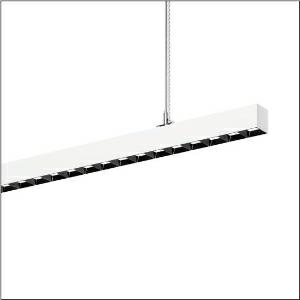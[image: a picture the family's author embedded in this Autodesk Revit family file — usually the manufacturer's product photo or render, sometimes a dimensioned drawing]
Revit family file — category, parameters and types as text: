
# Revit family: silica_r__21_51mx34dc3dwb_cbfc
name_source: partatom
category: Lighting Fixtures
units: mm (PartAtom-declared; Revit-internal decimal feet)

## family parameters
Cut with Voids When Loaded = No
Host = Face
Light Source = No
Part Type = Normal
Room Calculation Point = No
Round Connector Dimension = Use Diameter
Shared = No

## types (1)
- --- (1 x LED, 19200 lm, 129.1 W, 3000K)
    Apparent Load = 129 VA
    CIE Flux Codes = 74 94 99 56 100
    Color Rendering = 80
    Color Temperature = 3000K
    Default Elevation = 1800 mm
    Description = Silica® 21, office luminaire, primary light control with darklight reflector, of PMMA, black, light emission: direct/indirect distribution, primary light characteristic: asymmetric, installation type: suspended mounting, LED, rated luminous flux: 19.200lm, luminous efficacy: 149lm/W, light colour: 830, colour temperature: 3000K, control gear: DALI 2, with terminal, 3+2-pole, max. 2.5mm², mains connection: 220..240V, AC, 50/60Hz, rated input power: 129.1W, luminaire housing, of aluminium, traffic white (RAL 9016), length: 3.004mm, width: 53mm, height: 53mm, protection rating (complete): IP20, insulation class (complete): insulation class I (protective earthing), certification: CE, permissible operating ambient temperature: 0..+35°C, standard: EN 50419, packaging unit: 1 piece
    Height = 53 mm
    Lamp = 1 x LED
    Lamp Light Flux = 19200 lm
    Lamp Power = 129.1 W
    Lamp count = 1
    Length = 3004 mm
    Luminous efficacy = 149 lm/W
    Manufacturer = Siteco
    ModVariant = No
    Model = 51MX34DC3DWB
    Mounting Place = Ceiling
    Mounting Type = Pendant
    Number of Poles = 1
    OnlyDefault = Yes
    Power Factor = 1
    Product Name = Silica® 21
    Product group = office luminaire | ceiling pendant
    ProductGroupID = 903
    Protection Class = Protection class I
    Protection Degree = IP 20
    RLX_Detail_Level = 1
    RLX_Emergency_Light_Flux = 0 lm
    RLX_Emergency_Type = 0
    RLX_Emergency_Type_DB = No
    RlxData = <blob elided: 65373 chars, md5=e60156b5>
    Socket = socket
    Standby Power = 0 W
    System Light Flux = 19200 lm
    System Power = 129 W
    Type Comments = factory setting: luminous flux: 100 % | dim-lin: 254 | 448 mA
    Type Image = l_1335871.jpg
    URL = http://relux.com
    VarID = @adj_141783
    Voltage = 0 V
    Weight = 0.00 kg
    Width = 53 mm

## geometry (parser evidence)
native form markers: Blend x4, Sweep x12
no freeform markers — native parametric forms only
